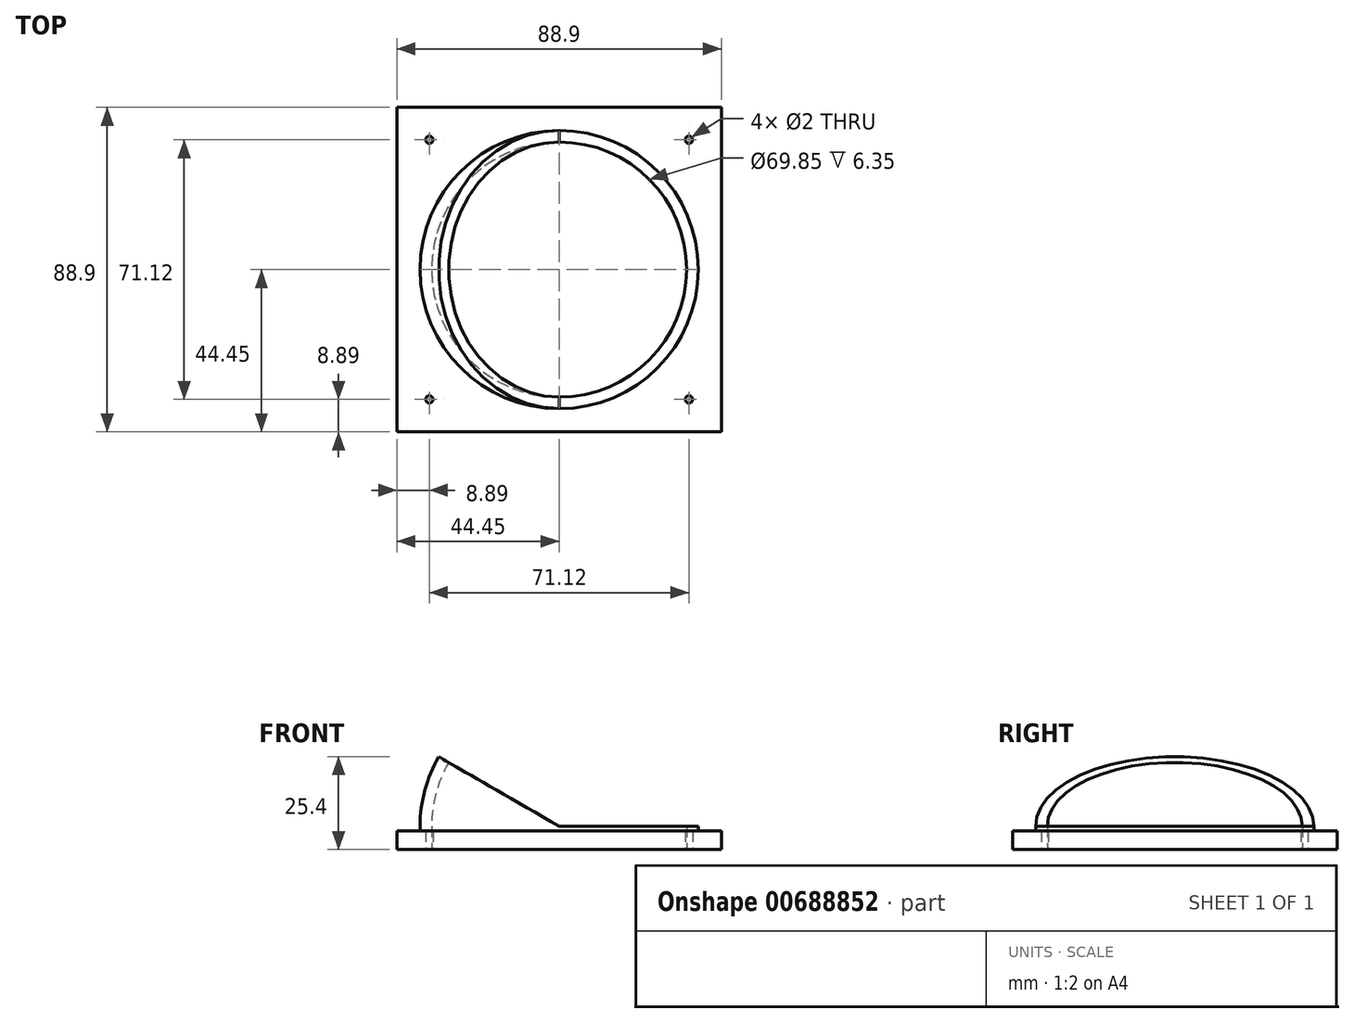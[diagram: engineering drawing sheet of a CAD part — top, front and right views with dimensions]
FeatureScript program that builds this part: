
annotation { "Feature Type Name" : "Feature", "Feature Type Description" : "" }
export const myFeature = defineFeature(function(context is Context, id is Id, definition is map)
    precondition{}
    {
        {
            var Q0;
            Q0=qCreatedBy(makeId("Top.planeOp"),FACE);
            var sketch = newSketch(context, id + "F0", { "sketchPlane" : qUnion([Q0])});
            skCircle(sketch, "E0", {"center": v(0, 0) * mm, "radius": 38.1 * mm});
            skLineSegment(sketch, "E1.bottom", {"start": v(-44.45, 44.45) * mm, "end": v(44.45, 44.45) * mm});
            skLineSegment(sketch, "E1.top", {"start": v(-44.45, -44.45) * mm, "end": v(44.45, -44.45) * mm});
            skLineSegment(sketch, "E1.left", {"start": v(-44.45, 44.45) * mm, "end": v(-44.45, -44.45) * mm});
            skLineSegment(sketch, "E1.right", {"start": v(44.45, 44.45) * mm, "end": v(44.45, -44.45) * mm});
            skCircle(sketch, "E2", {"center": v(0, 0) * mm, "radius": 34.93 * mm});
            skLineSegment(sketch, "E3", {"start": v(0, 38.1) * mm, "end": v(0, 34.93) * mm});
            skLineSegment(sketch, "E4", {"start": v(0, -34.93) * mm, "end": v(0, -38.1) * mm});
            skPoint(sketch, "E5", {"position": v(35.56, 35.56) * mm});
            skPoint(sketch, "E6", {"position": v(35.56, -35.56) * mm});
            skPoint(sketch, "E7", {"position": v(-35.56, -35.56) * mm});
            skPoint(sketch, "E8", {"position": v(-35.56, 35.56) * mm});
            skSolve(sketch);
        }
        {
            var Q0;
            Q0=makeQuery(id+"F0.imprint","IMPRINT",FACE,{"disambiguationData":[TD([[makeQuery(id+"F0.imprint","IMPRINT",EDGE,{"derivedFrom":sQuery(id+"F0.wireOp",EDGE,"E0")}),-1.0]])]});
            extrude(context, id + "F1", {"entities" : qUnion([Q0]), "depth" : 5.08 * mm, "offsetDistance" : 25.4 * mm});
        }
        {
            var Q0;
            {var subQ0=sQuery(id+"F0.wireOp",EDGE,"E3");Q0=makeQuery(id+"F0.imprint","IMPRINT",FACE,{"disambiguationData":[TD([[makeQuery(id+"F0.imprint","IMPRINT",EDGE,{"derivedFrom":subQ0}),-1.0]])]});}
            extrude(context, id + "F2", {"entities" : qUnion([Q0]), "operationType" : NewBodyOperationType.ADD, "depth" : 6.35 * mm, "offsetDistance" : 25.4 * mm});
        }
        {
            var Q0;
            {var subQ0=sQuery(id+"F0.wireOp",EDGE,"E3");Q0=makeQuery(id+"F0.imprint","IMPRINT",FACE,{"disambiguationData":[TD([[makeQuery(id+"F0.imprint","IMPRINT",EDGE,{"derivedFrom":subQ0}),1.0]])]});}
            extrude(context, id + "F3", {"entities" : qUnion([Q0]), "operationType" : NewBodyOperationType.ADD, "depth" : 6.35 * mm, "offsetDistance" : 25.4 * mm});
        }
        {
            var Q0;
            {var subQ0=sQuery(id+"F0.wireOp",EDGE,"E4");var subQ1=sQuery(id+"F0.wireOp",EDGE,"E3");var subQ2=sQuery(id+"F0.wireOp",EDGE,"E2");var subQ3=sQuery(id+"F0.wireOp",EDGE,"E0");Q0=makeQuery(id+"F3.boolean.opBoolean","MERGE",FACE,{"derivedFrom":[makeQuery(id+"F2.opExtrude","CAP_FACE",FACE,{"disambiguationData":[OSD([subQ3,subQ2,subQ1,subQ0])],"isStart":false}),makeQuery(id+"F3.opExtrude","CAP_FACE",FACE,{"disambiguationData":[OSD([subQ3,subQ2,subQ1,subQ0])],"isStart":false})]});}
            var sketch = newSketch(context, id + "F4", { "sketchPlane" : qUnion([Q0])});
            skLineSegment(sketch, "E9", {"start": v(0, -34.93) * mm, "end": v(0, -38.1) * mm});
            skLineSegment(sketch, "E10", {"start": v(0, 38.1) * mm, "end": v(0, 34.93) * mm});
            skSolve(sketch);
        }
        {
            var Q0;
            {var subQ0=sQuery(id+"F4.wireOp",EDGE,"E9");Q0=makeQuery(id+"F4.imprint","IMPRINT",FACE,{"disambiguationData":[TD([[makeQuery(id+"F4.imprint","IMPRINT",EDGE,{"derivedFrom":subQ0}),-1.0]])]});}
            var Q1;
            Q1=sQuery(id+"F4.wireOp",EDGE,"E9");
            revolve(context, id + "F5", {"operationType" : NewBodyOperationType.ADD, "surfaceOperationType" : NewSurfaceOperationType.NEW, "entities" : qUnion([Q0]), "axis" : qUnion([Q1]), "revolveType" : RevolveType.ONE_DIRECTION, "oppositeDirection" : true, "angle" : 30 * degree});
        }
        {
            var Q0;
            Q0=sQuery(id+"F0.wireOp",VERTEX,"E5");
            var Q1;
            Q1=sQuery(id+"F0.wireOp",VERTEX,"E6");
            var Q2;
            Q2=sQuery(id+"F0.wireOp",VERTEX,"E7");
            var Q3;
            Q3=sQuery(id+"F0.wireOp",VERTEX,"E8");
            var Q4;
            Q4=makeQuery(id+"F1.opExtrude","SWEPT_BODY",BODY,{"disambiguationData":[OSD([sQuery(id+"F0.wireOp",EDGE,"E0"),sQuery(id+"F0.wireOp",EDGE,"E1.bottom"),sQuery(id+"F0.wireOp",EDGE,"E1.top"),sQuery(id+"F0.wireOp",EDGE,"E1.left"),sQuery(id+"F0.wireOp",EDGE,"E1.right")])]});
            hole(context, id + "F6", {"style" : HoleStyle.SIMPLE, "endStyle" : HoleEndStyle.THROUGH, "oppositeDirection" : true, "holeDiameter" : 2 * mm, "majorDiameter" : 6.35 * mm, "isTappedThrough" : true, "tappedDepth" : 12.7 * mm, "tapClearance" : 3, "startFromSketch" : true, "locations" : qUnion([Q0, Q1, Q2, Q3]), "scope" : qUnion([Q4])});
        }
    });
